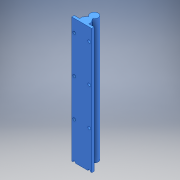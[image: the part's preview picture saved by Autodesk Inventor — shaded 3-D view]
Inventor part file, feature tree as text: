
AUTODESK INVENTOR PART (.ipt)
format: ipt  version: 2018 (Build 220112000, 112)  size: 158,208 bytes
history: native  units: mm
features: other x1, extrude x1, hole x1, sketch x1
ambient origin geometry x8: Origin, YZ Plane, XZ Plane, XY Plane, X Axis, Y Axis, Z Axis, Center Point
bodies: Body1 (feature_tree)
feature tree (4):
  other  "Sólido1"
  extrude  "Extrusão1"  Depth=8.0mm
  hole  "Furo2"  [1 undecoded]
  sketch  "Esboço1"  dims[d6=16.0mm d7=25.0mm d8=18.5mm d9=11.7mm d10=8.0mm d11=30.0deg d12=30.0deg d13=5.0mm d14=40.0mm d15=250.0mm d16=0.0mm d18=15.0mm d19=15.0mm d20=5.5mm d21=5.5mm d22=25.0mm d35=40.0mm d37=75.0mm d38=10.0mm d40=10.0mm d42=40.0mm d44=75.0mm d45=10.0mm d47=10.0mm d49=5.5mm d50=6.0mm d51=4.0mm d52=2.0mm d53=90.0deg d54=8.0mm d55=20.594885mm]
note: 1 required parameter value undecoded (feature->parameter linkage not recoverable at this tier; creation-order binding heuristic only, values carry confidence <= 0.55)
